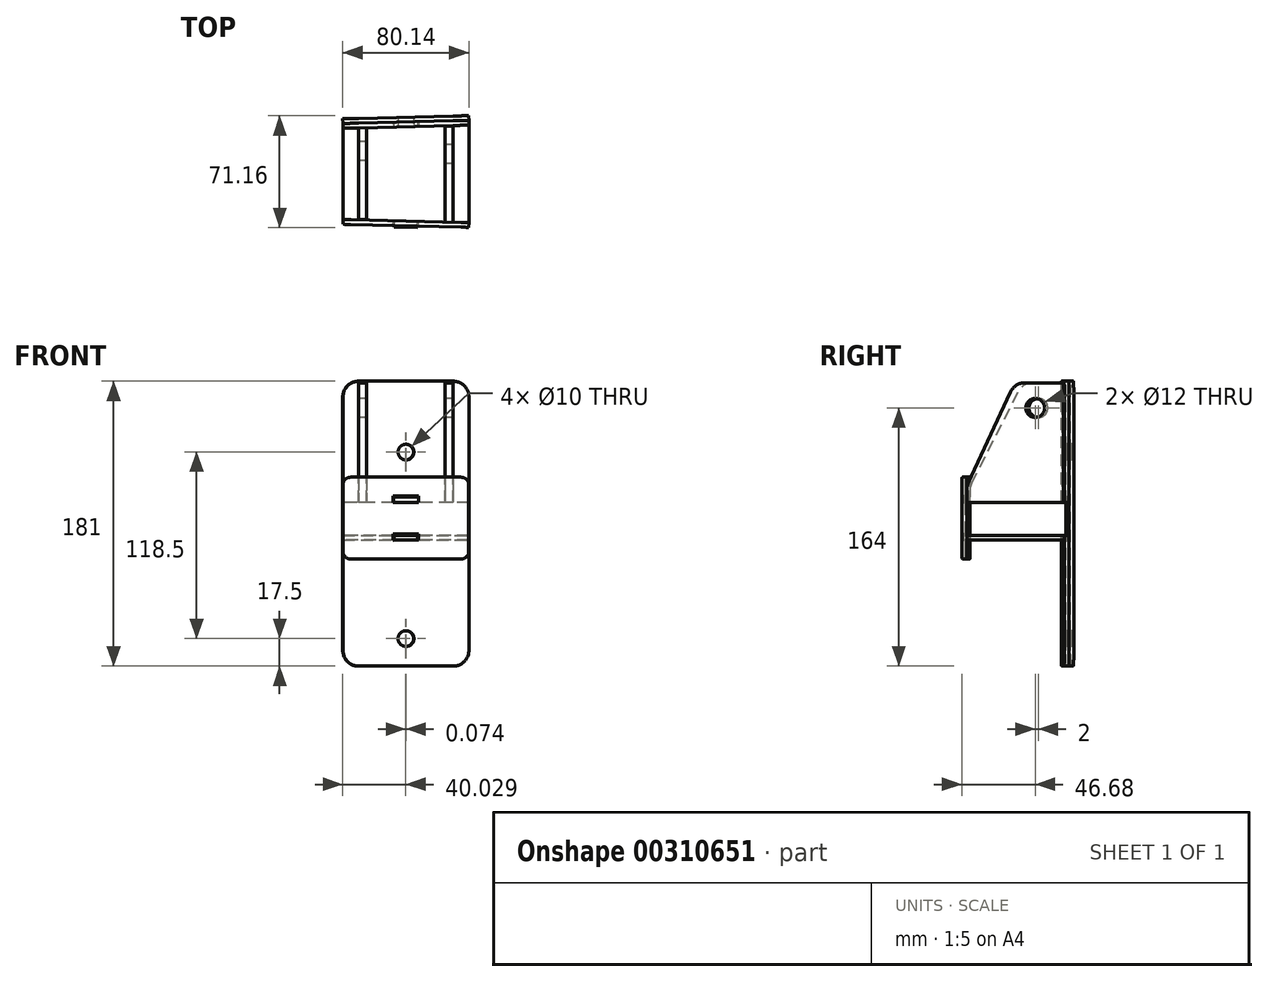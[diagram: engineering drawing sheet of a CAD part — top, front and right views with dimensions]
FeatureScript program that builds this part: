
annotation { "Feature Type Name" : "Feature", "Feature Type Description" : "" }
export const myFeature = defineFeature(function(context is Context, id is Id, definition is map)
    precondition{}
    {
        {
            var Q0;
            Q0=qCreatedBy(makeId("Top.planeOp"),FACE);
            var sketch = newSketch(context, id + "F0", { "sketchPlane" : qUnion([Q0])});
            skLineSegment(sketch, "E0", {"start": v(0, 58) * mm, "end": v(0, 0) * mm});
            skLineSegment(sketch, "E1", {"start": v(0, 0) * mm, "end": v(32.5, -0.8) * mm});
            skLineSegment(sketch, "E2", {"start": v(80, -1.98) * mm, "end": v(80, 59.98) * mm});
            skLineSegment(sketch, "E3", {"start": v(80, 59.98) * mm, "end": v(47.5, 59.18) * mm});
            skLineSegment(sketch, "E4", {"start": v(32.5, -0.8) * mm, "end": v(32.4, -4.8) * mm});
            skLineSegment(sketch, "E5", {"start": v(32.4, -4.8) * mm, "end": v(47.4, -5.18) * mm});
            skLineSegment(sketch, "E6", {"start": v(47.4, -5.18) * mm, "end": v(47.5, -1.18) * mm});
            skLineSegment(sketch, "E7", {"start": v(32.5, 58.8) * mm, "end": v(32.43, 61.8) * mm});
            skLineSegment(sketch, "E8", {"start": v(32.43, 61.8) * mm, "end": v(47.42, 62.18) * mm});
            skLineSegment(sketch, "E9", {"start": v(47.42, 62.18) * mm, "end": v(47.5, 59.18) * mm});
            skLineSegment(sketch, "E10.trimOffspring", {"start": v(32.5, 58.8) * mm, "end": v(0, 58) * mm});
            skLineSegment(sketch, "E11.trimOffspring", {"start": v(47.5, -1.18) * mm, "end": v(80, -1.98) * mm});
            skSolve(sketch);
        }
        {
            var Q0;
            Q0=qSketchRegion(id+"F0",true);
            extrude(context, id + "F1", {"entities" : qUnion([Q0]), "depth" : 3 * mm});
        }
        {
            var Q0;
            Q0=makeQuery(id+"F1.opExtrude","SWEPT_FACE",FACE,{"disambiguationData":[OSD([sQuery(id+"F0.wireOp",EDGE,"E1")])]});
            var sketch = newSketch(context, id + "F2", { "sketchPlane" : qUnion([Q0])});
            skLineSegment(sketch, "E12.bottom", {"start": v(5, -12) * mm, "end": v(75, -12) * mm});
            skLineSegment(sketch, "E12.top", {"start": v(5, 40) * mm, "end": v(75, 40) * mm});
            skLineSegment(sketch, "E12.left", {"start": v(0, -7) * mm, "end": v(0, 35) * mm});
            skLineSegment(sketch, "E12.right", {"start": v(80, -7) * mm, "end": v(80, 35) * mm});
            skLineSegment(sketch, "E13.bottom", {"start": v(32, 0) * mm, "end": v(48, 0) * mm});
            skLineSegment(sketch, "E13.top", {"start": v(32, 4) * mm, "end": v(48, 4) * mm});
            skLineSegment(sketch, "E13.left", {"start": v(32, 0) * mm, "end": v(32, 4) * mm});
            skLineSegment(sketch, "E13.right", {"start": v(48, 0) * mm, "end": v(48, 4) * mm});
            skLineSegment(sketch, "E14.bottom", {"start": v(32, 28) * mm, "end": v(48, 28) * mm});
            skLineSegment(sketch, "E14.top", {"start": v(32, 24) * mm, "end": v(48, 24) * mm});
            skLineSegment(sketch, "E14.left", {"start": v(32, 28) * mm, "end": v(32, 24) * mm});
            skLineSegment(sketch, "E14.right", {"start": v(48, 28) * mm, "end": v(48, 24) * mm});
            skPoint(sketch, "E15.visualSharp", {"position": v(80, 40) * mm});
            skArc(sketch, "E15.filletArc", {"start": v(80, 35) * mm, "mid": v(78.54, 38.54) * mm, "end": v(75, 40) * mm});
            skPoint(sketch, "E16.visualSharp", {"position": v(0, 40) * mm});
            skArc(sketch, "E16.filletArc", {"start": v(5, 40) * mm, "mid": v(1.46, 38.54) * mm, "end": v(0, 35) * mm});
            skPoint(sketch, "E17.visualSharp", {"position": v(0, -12) * mm});
            skArc(sketch, "E17.filletArc", {"start": v(0, -7) * mm, "mid": v(1.46, -10.54) * mm, "end": v(5, -12) * mm});
            skPoint(sketch, "E18.visualSharp", {"position": v(80, -12) * mm});
            skArc(sketch, "E18.filletArc", {"start": v(75, -12) * mm, "mid": v(78.54, -10.54) * mm, "end": v(80, -7) * mm});
            skSolve(sketch);
        }
        {
            var Q0;
            Q0=qSketchRegion(id+"F2",true);
            extrude(context, id + "F3", {"entities" : qUnion([Q0]), "depth" : 3 * mm});
        }
        {
            var Q0;
            Q0=makeQuery(id+"F1.opExtrude","SWEPT_FACE",FACE,{"disambiguationData":[OSD([sQuery(id+"F0.wireOp",EDGE,"E10.trimOffspring")])]});
            var sketch = newSketch(context, id + "F4", { "sketchPlane" : qUnion([Q0])});
            skLineSegment(sketch, "E19.bottom", {"start": v(-71.45, -80) * mm, "end": v(-11.45, -80) * mm});
            skLineSegment(sketch, "E19.top", {"start": v(-71.45, 101) * mm, "end": v(-11.45, 101) * mm});
            skLineSegment(sketch, "E19.left", {"start": v(-81.45, -70) * mm, "end": v(-81.45, 3) * mm});
            skLineSegment(sketch, "E19.right", {"start": v(-1.45, -70) * mm, "end": v(-1.45, 3) * mm});
            skLineSegment(sketch, "E20.bottom", {"start": v(-49.45, 27.5) * mm, "end": v(-33.45, 27.5) * mm});
            skLineSegment(sketch, "E20.top", {"start": v(-81.45, 24) * mm, "end": v(-49.45, 24) * mm});
            skLineSegment(sketch, "E20.left", {"start": v(-49.45, 27.5) * mm, "end": v(-49.45, 24) * mm});
            skLineSegment(sketch, "E20.right", {"start": v(-33.45, 27.5) * mm, "end": v(-33.45, 24) * mm});
            skLineSegment(sketch, "E21.bottom", {"start": v(-81.45, 3) * mm, "end": v(-49.45, 3) * mm});
            skLineSegment(sketch, "E21.top", {"start": v(-49.45, -0.5) * mm, "end": v(-33.45, -0.5) * mm});
            skLineSegment(sketch, "E21.left", {"start": v(-49.45, 3) * mm, "end": v(-49.45, -0.5) * mm});
            skLineSegment(sketch, "E21.right", {"start": v(-33.45, 3) * mm, "end": v(-33.45, -0.5) * mm});
            skLineSegment(sketch, "E22.trimOffspring", {"start": v(-33.45, 24) * mm, "end": v(-1.45, 24) * mm});
            skLineSegment(sketch, "E23.trimOffspring", {"start": v(-81.45, 24) * mm, "end": v(-81.45, 91) * mm});
            skLineSegment(sketch, "E24.trimOffspring", {"start": v(-1.45, 24) * mm, "end": v(-1.45, 91) * mm});
            skLineSegment(sketch, "E25.trimOffspring", {"start": v(-33.45, 3) * mm, "end": v(-1.45, 3) * mm});
            skCircle(sketch, "E26", {"center": v(-41.45, 56) * mm, "radius": 5 * mm});
            skCircle(sketch, "E27", {"center": v(-41.45, -62.5) * mm, "radius": 5 * mm});
            skPoint(sketch, "E28.visualSharp", {"position": v(-81.45, 101) * mm});
            skArc(sketch, "E28.filletArc", {"start": v(-71.45, 101) * mm, "mid": v(-78.52, 98.07) * mm, "end": v(-81.45, 91) * mm});
            skPoint(sketch, "E29.visualSharp", {"position": v(-1.45, 101) * mm});
            skArc(sketch, "E29.filletArc", {"start": v(-1.45, 91) * mm, "mid": v(-4.38, 98.07) * mm, "end": v(-11.45, 101) * mm});
            skPoint(sketch, "E30.visualSharp", {"position": v(-81.45, -80) * mm});
            skArc(sketch, "E30.filletArc", {"start": v(-81.45, -70) * mm, "mid": v(-78.52, -77.07) * mm, "end": v(-71.45, -80) * mm});
            skPoint(sketch, "E31.visualSharp", {"position": v(-1.45, -80) * mm});
            skArc(sketch, "E31.filletArc", {"start": v(-11.45, -80) * mm, "mid": v(-4.38, -77.07) * mm, "end": v(-1.45, -70) * mm});
            skSolve(sketch);
        }
        {
            var Q0;
            Q0=qSketchRegion(id+"F4",true);
            extrude(context, id + "F5", {"entities" : qUnion([Q0]), "depth" : 3 * mm});
        }
        {
            var Q0;
            Q0=makeQuery(id+"F5.opExtrude","CAP_FACE",FACE,{"disambiguationData":[OSD([sQuery(id+"F4.wireOp",EDGE,"E19.top"),sQuery(id+"F4.wireOp",EDGE,"E20.bottom"),sQuery(id+"F4.wireOp",EDGE,"E20.top"),sQuery(id+"F4.wireOp",EDGE,"E20.left"),sQuery(id+"F4.wireOp",EDGE,"E20.right"),sQuery(id+"F4.wireOp",EDGE,"E22.trimOffspring"),sQuery(id+"F4.wireOp",EDGE,"E23.trimOffspring"),sQuery(id+"F4.wireOp",EDGE,"E24.trimOffspring"),sQuery(id+"F4.wireOp",EDGE,"E26")])],"isStart":false});
            var sketch = newSketch(context, id + "F6", { "sketchPlane" : qUnion([Q0])});
            skLineSegment(sketch, "E32.bottom", {"start": v(-71.45, -80) * mm, "end": v(-11.45, -80) * mm});
            skLineSegment(sketch, "E32.top", {"start": v(-71.45, 101) * mm, "end": v(-11.45, 101) * mm});
            skLineSegment(sketch, "E32.left", {"start": v(-81.45, -70) * mm, "end": v(-81.45, 91) * mm});
            skLineSegment(sketch, "E32.right", {"start": v(-1.45, -70) * mm, "end": v(-1.45, 91) * mm});
            skLineSegment(sketch, "E33.bottom", {"start": v(-81.45, 35.5) * mm, "end": v(-1.45, 35.5) * mm, "construction": true});
            skLineSegment(sketch, "E33.top", {"start": v(-81.45, -14.5) * mm, "end": v(-1.45, -14.5) * mm, "construction": true});
            skLineSegment(sketch, "E33.left", {"start": v(-81.45, 35.5) * mm, "end": v(-81.45, -14.5) * mm, "construction": true});
            skLineSegment(sketch, "E33.right", {"start": v(-1.45, 35.5) * mm, "end": v(-1.45, -14.5) * mm, "construction": true});
            skPoint(sketch, "E34", {"position": v(-41.45, 35.5) * mm});
            skPoint(sketch, "E35", {"position": v(-41.45, -14.5) * mm});
            skLineSegment(sketch, "E36", {"start": v(-41.45, 101) * mm, "end": v(-41.45, 35.5) * mm, "construction": true});
            skLineSegment(sketch, "E37", {"start": v(-41.45, -14.5) * mm, "end": v(-41.45, 35.5) * mm, "construction": true});
            skLineSegment(sketch, "E38", {"start": v(-41.45, -14.5) * mm, "end": v(-41.45, -80) * mm, "construction": true});
            skCircle(sketch, "E39", {"center": v(-41.45, -62.5) * mm, "radius": 5 * mm});
            skPoint(sketch, "E39.centerSnap0", {"position": v(-41.45, 101) * mm});
            skCircle(sketch, "E40", {"center": v(-41.45, 56) * mm, "radius": 5 * mm});
            skPoint(sketch, "E41.visualSharp", {"position": v(-81.45, 101) * mm});
            skArc(sketch, "E41.filletArc", {"start": v(-71.45, 101) * mm, "mid": v(-78.52, 98.07) * mm, "end": v(-81.45, 91) * mm});
            skPoint(sketch, "E42.visualSharp", {"position": v(-1.45, 101) * mm});
            skArc(sketch, "E42.filletArc", {"start": v(-1.45, 91) * mm, "mid": v(-4.38, 98.07) * mm, "end": v(-11.45, 101) * mm});
            skPoint(sketch, "E43.visualSharp", {"position": v(-1.45, -80) * mm});
            skArc(sketch, "E43.filletArc", {"start": v(-11.45, -80) * mm, "mid": v(-4.38, -77.07) * mm, "end": v(-1.45, -70) * mm});
            skPoint(sketch, "E44.visualSharp", {"position": v(-81.45, -80) * mm});
            skArc(sketch, "E44.filletArc", {"start": v(-81.45, -70) * mm, "mid": v(-78.52, -77.07) * mm, "end": v(-71.45, -80) * mm});
            skSolve(sketch);
        }
        {
            var Q0;
            Q0=qSketchRegion(id+"F6",true);
            extrude(context, id + "F7", {"entities" : qUnion([Q0]), "depth" : 3 * mm});
        }
        {
            var Q0;
            Q0=qCreatedBy(makeId("Right.planeOp"),FACE);
            var sketch = newSketch(context, id + "F8", { "sketchPlane" : qUnion([Q0])});
            skLineSegment(sketch, "E45.top", {"start": v(58.5, 24) * mm, "end": v(0, 24) * mm});
            skLineSegment(sketch, "E45.left", {"start": v(58.5, 99) * mm, "end": v(58.5, 24) * mm});
            skLineSegment(sketch, "E46", {"start": v(0, 24) * mm, "end": v(0, 31.6) * mm});
            skLineSegment(sketch, "E47", {"start": v(1.1, 36.14) * mm, "end": v(30.92, 94.55) * mm});
            skPoint(sketch, "E48.visualSharp", {"position": v(0, 34) * mm});
            skArc(sketch, "E48.filletArc", {"start": v(1.1, 36.14) * mm, "mid": v(0.28, 33.93) * mm, "end": v(0, 31.6) * mm});
            skCircle(sketch, "E49", {"center": v(43.5, 84) * mm, "radius": 6 * mm});
            skLineSegment(sketch, "E50", {"start": v(39.83, 100) * mm, "end": v(57.5, 100) * mm});
            skPoint(sketch, "E51.visualSharp", {"position": v(33.7, 100) * mm});
            skArc(sketch, "E51.filletArc", {"start": v(39.83, 100) * mm, "mid": v(34.6, 98.53) * mm, "end": v(30.92, 94.55) * mm});
            skPoint(sketch, "E52.visualSharp", {"position": v(58.5, 100) * mm});
            skArc(sketch, "E52.filletArc", {"start": v(58.5, 99) * mm, "mid": v(58.2, 99.7) * mm, "end": v(57.5, 100) * mm});
            skSolve(sketch);
        }
        {
            var Q0;
            Q0=qSketchRegion(id+"F8",true);
            extrude(context, id + "F9", {"entities" : qUnion([Q0]), "depth" : 5 * mm});
        }
        {
            var Q0;
            Q0=makeQuery(id+"F9.opExtrude","SWEPT_BODY",BODY,{"disambiguationData":[OSD([sQuery(id+"F8.wireOp",EDGE,"E45.top"),sQuery(id+"F8.wireOp",EDGE,"E45.left"),sQuery(id+"F8.wireOp",EDGE,"E46"),sQuery(id+"F8.wireOp",EDGE,"E47")])]});
            transform(context, id + "F10", {"entities" : qUnion([Q0]), "transformType" : TransformType.TRANSLATION_3D, "dx" : 10 * mm, "dy" : 0 * mm, "dz" : 0 * mm, "makeCopy" : false});
        }
        {
            var Q0;
            Q0=qCreatedBy(makeId("Right.planeOp"),FACE);
            var sketch = newSketch(context, id + "F11", { "sketchPlane" : qUnion([Q0])});
            skLineSegment(sketch, "E53", {"start": v(0, 24) * mm, "end": v(61.5, 24) * mm});
            skLineSegment(sketch, "E54", {"start": v(61.5, 24) * mm, "end": v(61.5, 100) * mm});
            skLineSegment(sketch, "E55", {"start": v(27.83, 94.2) * mm, "end": v(0.92, 36) * mm});
            skLineSegment(sketch, "E56", {"start": v(0, 31.8) * mm, "end": v(0, 24) * mm});
            skPoint(sketch, "E57.visualSharp", {"position": v(0, 34) * mm});
            skArc(sketch, "E57.filletArc", {"start": v(0.92, 36) * mm, "mid": v(0.23, 33.95) * mm, "end": v(0, 31.8) * mm});
            skLineSegment(sketch, "E58", {"start": v(36.9, 100) * mm, "end": v(61.5, 100) * mm});
            skCircle(sketch, "E59", {"center": v(43.5, 84) * mm, "radius": 6 * mm});
            skPoint(sketch, "E60.visualSharp", {"position": v(30.52, 100) * mm});
            skArc(sketch, "E60.filletArc", {"start": v(36.9, 100) * mm, "mid": v(31.52, 98.43) * mm, "end": v(27.83, 94.2) * mm});
            skSolve(sketch);
        }
        {
            var Q0;
            Q0=qSketchRegion(id+"F11",true);
            extrude(context, id + "F12", {"entities" : qUnion([Q0]), "depth" : 5 * mm});
        }
        {
            var Q0;
            Q0=makeQuery(id+"F12.opExtrude","SWEPT_BODY",BODY,{"disambiguationData":[OSD([sQuery(id+"F11.wireOp",EDGE,"E53"),sQuery(id+"F11.wireOp",EDGE,"E54"),sQuery(id+"F11.wireOp",EDGE,"E55"),sQuery(id+"F11.wireOp",EDGE,"E56")])]});
            transform(context, id + "F13", {"entities" : qUnion([Q0]), "transformType" : TransformType.TRANSLATION_3D, "dx" : 65 * mm, "dy" : -2 * mm, "dz" : 0 * mm, "makeCopy" : false});
        }
    });
